# Revit family: Bathtub-Freestanding-DXV-Lyndon-D12536004
name_source: partatom
category: Plumbing Fixtures
revit_build: Autodesk Revit 2014 (Build: 20130308_1515(x64)
units: mm (PartAtom-declared; Revit-internal decimal feet)

## types (1)
- D12536004.415
    Assembly Code = D2010510
    Body Material = Acrylic-DXC-415-Canvas White
    CW Connection = No
    CWFU = 5
    Default Elevation = 0"
    Description = Free Standing Center Drain Soaker - CWH
    HW Connection = No
    HWFU = 0
    Height = 24 1/2"
    Installation Type = Floor Mounted
    Length = 30 1/2"
    Manufacturer = DXV
    Material = Acrylic-DXC-415-Canvas White
    Model = D12536.004
    Price = Prices may vary. Please consult manufacturer representative for most up to date price list.
    Product Documentation Link = https://dxv01.blob.core.windows.net
    Product Page URL = https://www.dxv.com
    URL = www.dxv.com
    Vent Connection = No
    WFU = 5
    Waste Connection = Yes
    Waste Connection Diameter = 2 1/2"
    Waste Connection Radius = 1 1/2"
    Width = 67"

## geometry (parser evidence)
native form markers: Sweep x1
no freeform markers — native parametric forms only
